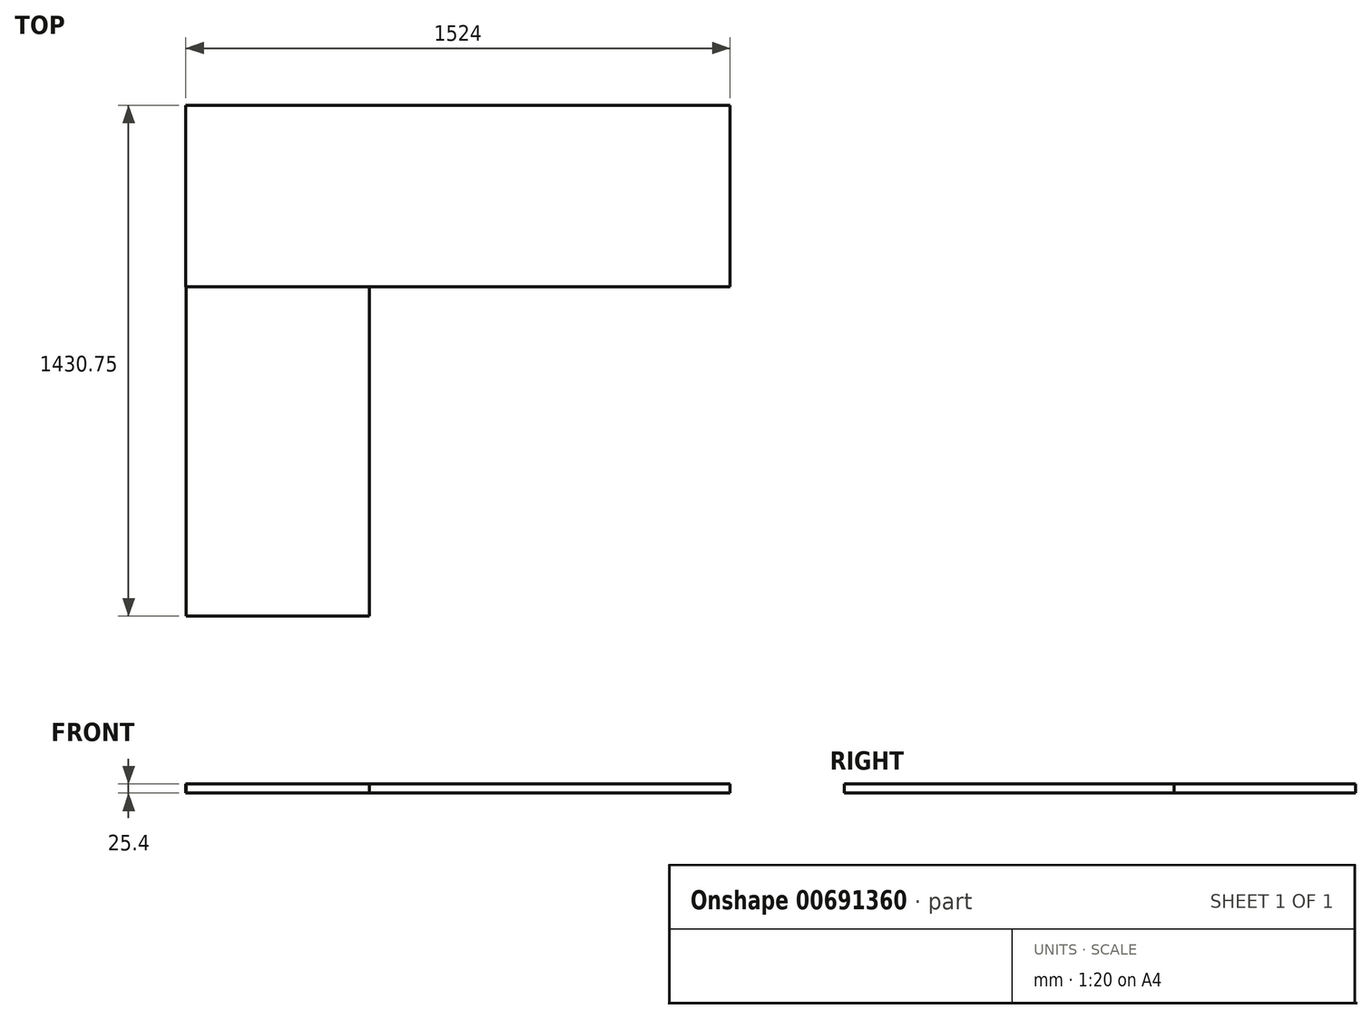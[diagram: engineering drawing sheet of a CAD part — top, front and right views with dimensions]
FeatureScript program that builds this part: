
annotation { "Feature Type Name" : "Feature", "Feature Type Description" : "" }
export const myFeature = defineFeature(function(context is Context, id is Id, definition is map)
    precondition{}
    {
        {
            var Q0;
            Q0=qCreatedBy(makeId("Top.planeOp"),FACE);
            var sketch = newSketch(context, id + "F0", { "sketchPlane" : qUnion([Q0])});
            skLineSegment(sketch, "E0.bottom", {"start": v(-596.64, 381.38) * mm, "end": v(927.36, 381.38) * mm});
            skLineSegment(sketch, "E0.top", {"start": v(-596.64, -126.62) * mm, "end": v(927.36, -126.62) * mm});
            skLineSegment(sketch, "E0.left", {"start": v(-596.64, 381.38) * mm, "end": v(-596.64, -126.62) * mm});
            skLineSegment(sketch, "E0.right", {"start": v(927.36, 381.38) * mm, "end": v(927.36, -126.62) * mm});
            skSolve(sketch);
        }
        {
            var Q0;
            Q0=makeQuery(id+"F0.imprint","IMPRINT",FACE,{"disambiguationData":[TD([[makeQuery(id+"F0.imprint","IMPRINT",EDGE,{"derivedFrom":sQuery(id+"F0.wireOp",EDGE,"E0.bottom")}),-1.0]])]});
            var sketch = newSketch(context, id + "F1", { "sketchPlane" : qUnion([Q0])});
            skLineSegment(sketch, "E1.bottom", {"start": v(-596.2, -126.16) * mm, "end": v(-83.41, -126.16) * mm});
            skLineSegment(sketch, "E1.top", {"start": v(-596.2, -1049.37) * mm, "end": v(-83.41, -1049.37) * mm});
            skLineSegment(sketch, "E1.left", {"start": v(-596.2, -126.16) * mm, "end": v(-596.2, -1049.37) * mm});
            skLineSegment(sketch, "E1.right", {"start": v(-83.41, -126.16) * mm, "end": v(-83.41, -1049.37) * mm});
            skSolve(sketch);
        }
        {
            var Q0;
            {var subQ0=sQuery(id+"F1.wireOp",EDGE,"E1.top");Q0=makeQuery(id+"F1.imprint","IMPRINT",FACE,{"disambiguationData":[TD([[makeQuery(id+"F1.imprint","IMPRINT",EDGE,{"derivedFrom":subQ0}),1.0]])]});}
            var Q1;
            Q1=makeQuery(id+"F0.imprint","IMPRINT",FACE,{"disambiguationData":[TD([[makeQuery(id+"F0.imprint","IMPRINT",EDGE,{"derivedFrom":sQuery(id+"F0.wireOp",EDGE,"E0.bottom")}),-1.0]])]});
            extrude(context, id + "F2", {"entities" : qUnion([Q0, Q1]), "depth" : 25.4 * mm, "offsetDistance" : 25.4 * mm});
        }
    });
